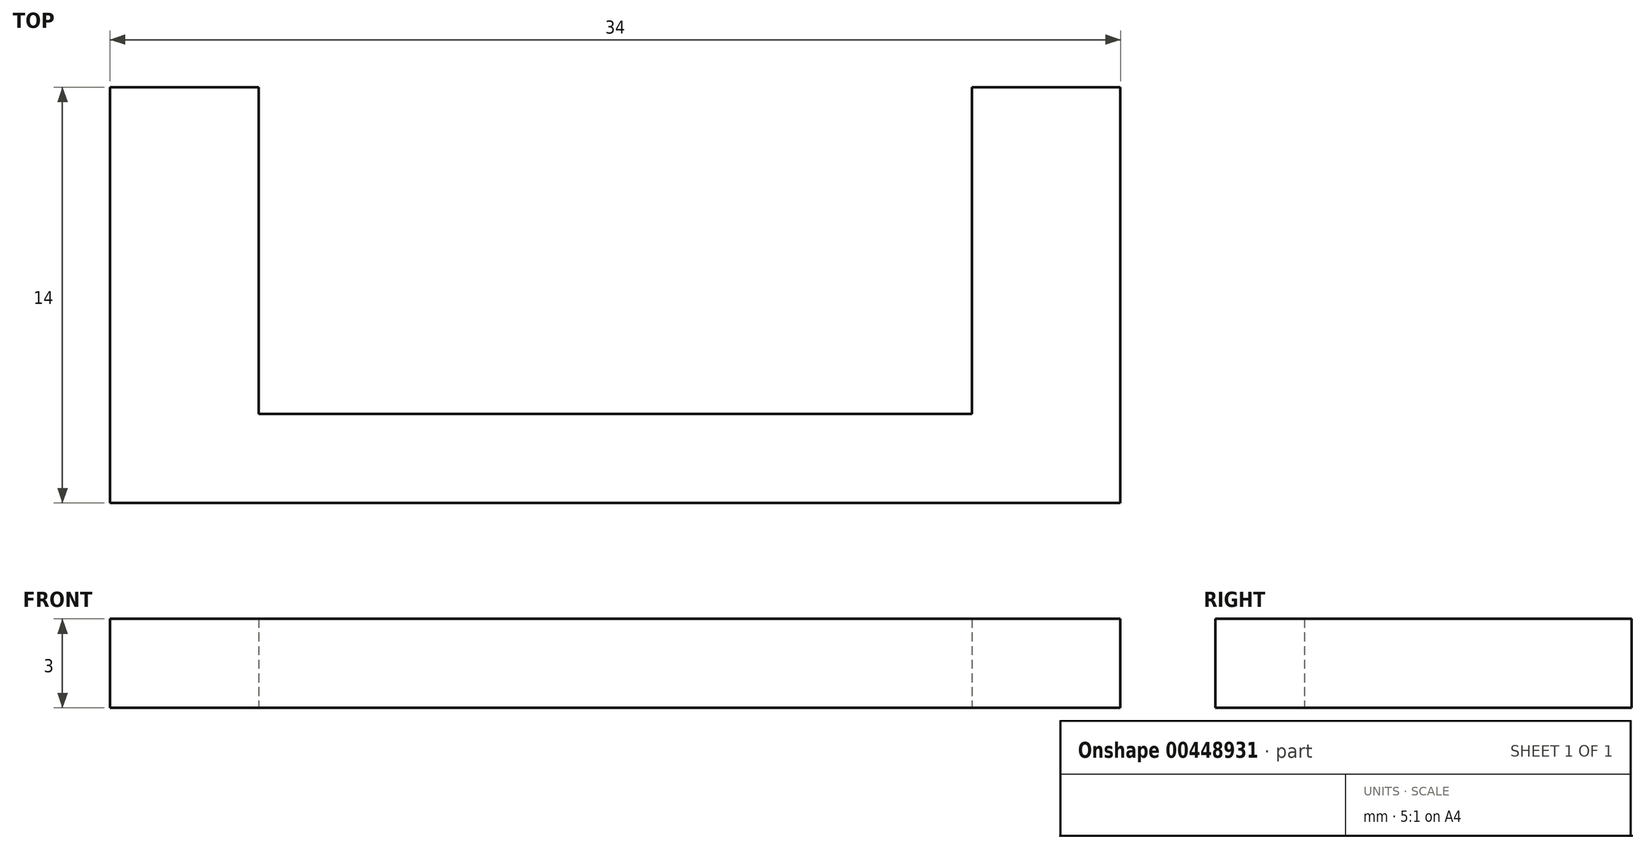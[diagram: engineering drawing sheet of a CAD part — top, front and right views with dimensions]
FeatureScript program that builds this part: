
annotation { "Feature Type Name" : "Feature", "Feature Type Description" : "" }
export const myFeature = defineFeature(function(context is Context, id is Id, definition is map)
    precondition{}
    {
        {
            var Q0;
            Q0=qCreatedBy(makeId("Top.planeOp"),FACE);
            var sketch = newSketch(context, id + "F0", { "sketchPlane" : qUnion([Q0])});
            skLineSegment(sketch, "E0.bottom", {"start": v(9.27, -13.95) * mm, "end": v(43.27, -13.95) * mm});
            skLineSegment(sketch, "E0.top", {"start": v(9.27, -16.95) * mm, "end": v(43.27, -16.95) * mm});
            skLineSegment(sketch, "E0.left", {"start": v(9.27, -13.95) * mm, "end": v(9.27, -16.95) * mm});
            skLineSegment(sketch, "E0.right", {"start": v(43.27, -13.95) * mm, "end": v(43.27, -16.95) * mm});
            skLineSegment(sketch, "E1.bottom", {"start": v(9.27, -16.95) * mm, "end": v(14.27, -16.95) * mm});
            skLineSegment(sketch, "E1.top", {"start": v(9.27, -2.95) * mm, "end": v(14.27, -2.95) * mm});
            skLineSegment(sketch, "E1.left", {"start": v(9.27, -16.95) * mm, "end": v(9.27, -2.95) * mm});
            skLineSegment(sketch, "E1.right", {"start": v(14.27, -16.95) * mm, "end": v(14.27, -2.95) * mm});
            skLineSegment(sketch, "E2.bottom", {"start": v(43.27, -16.95) * mm, "end": v(38.27, -16.95) * mm});
            skLineSegment(sketch, "E2.top", {"start": v(43.27, -2.95) * mm, "end": v(38.27, -2.95) * mm});
            skLineSegment(sketch, "E2.left", {"start": v(43.27, -16.95) * mm, "end": v(43.27, -2.95) * mm});
            skLineSegment(sketch, "E2.right", {"start": v(38.27, -16.95) * mm, "end": v(38.27, -2.95) * mm});
            skSolve(sketch);
        }
        {
            var Q0;
            {var subQ5=sQuery(id+"F0.wireOp",EDGE,"E1.top");Q0=makeQuery(id+"F0.imprint","IMPRINT",FACE,{"disambiguationData":[TD([[makeQuery(id+"F0.imprint","IMPRINT",EDGE,{"derivedFrom":subQ5}),-1.0]])]});}
            var Q1;
            {var subQ5=sQuery(id+"F0.wireOp",EDGE,"E1.bottom");Q1=makeQuery(id+"F0.imprint","IMPRINT",FACE,{"disambiguationData":[TD([[makeQuery(id+"F0.imprint","IMPRINT",EDGE,{"derivedFrom":subQ5}),1.0]])]});}
            var Q2;
            {var subQ5=sQuery(id+"F0.wireOp",EDGE,"E0.top");Q2=makeQuery(id+"F0.imprint","IMPRINT",FACE,{"disambiguationData":[TD([[makeQuery(id+"F0.imprint","IMPRINT",EDGE,{"derivedFrom":subQ5}),1.0]])]});}
            var Q3;
            {var subQ5=sQuery(id+"F0.wireOp",EDGE,"E2.bottom");Q3=makeQuery(id+"F0.imprint","IMPRINT",FACE,{"disambiguationData":[TD([[makeQuery(id+"F0.imprint","IMPRINT",EDGE,{"derivedFrom":subQ5}),-1.0]])]});}
            var Q4;
            {var subQ5=sQuery(id+"F0.wireOp",EDGE,"E2.top");Q4=makeQuery(id+"F0.imprint","IMPRINT",FACE,{"disambiguationData":[TD([[makeQuery(id+"F0.imprint","IMPRINT",EDGE,{"derivedFrom":subQ5}),1.0]])]});}
            extrude(context, id + "F1", {"entities" : qUnion([Q0, Q1, Q2, Q3, Q4]), "depth" : 3 * mm});
        }
    });
